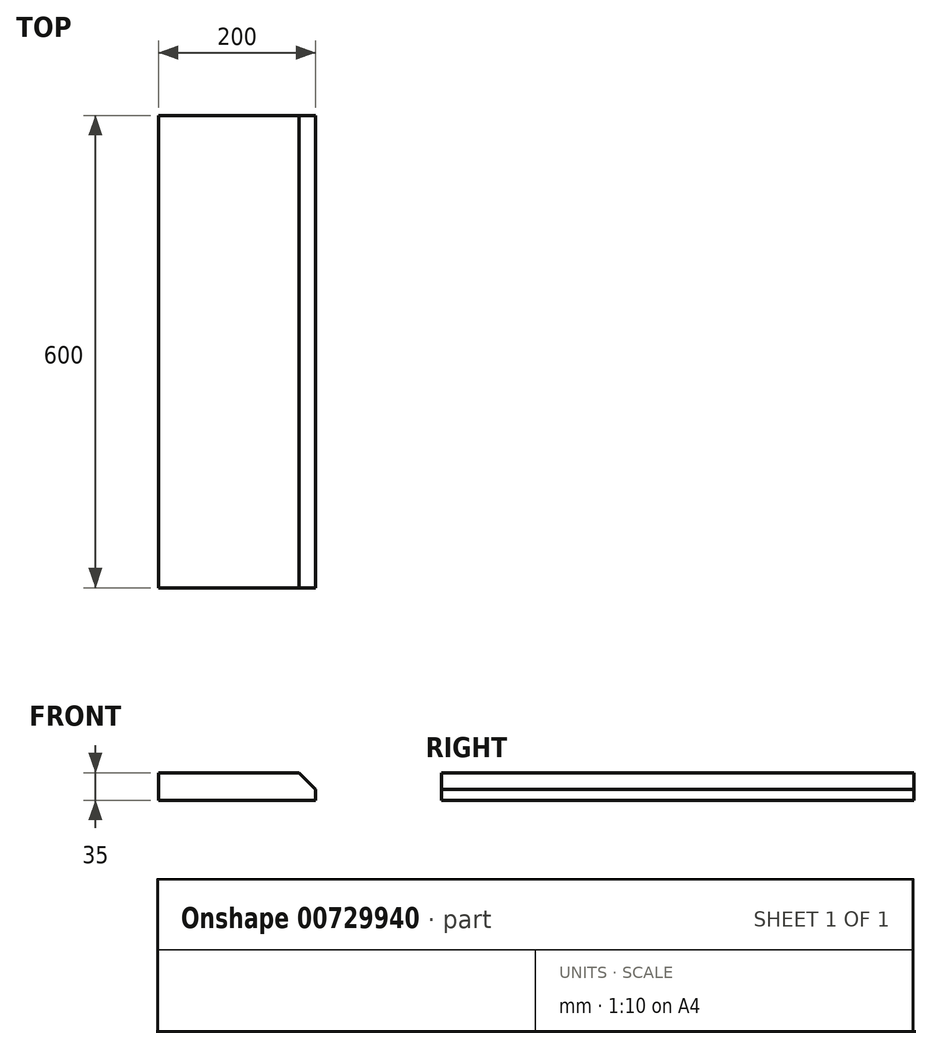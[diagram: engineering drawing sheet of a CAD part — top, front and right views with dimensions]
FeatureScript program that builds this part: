
annotation { "Feature Type Name" : "Feature", "Feature Type Description" : "" }
export const myFeature = defineFeature(function(context is Context, id is Id, definition is map)
    precondition{}
    {
        {
            var Q0;
            Q0=qCreatedBy(makeId("Front.planeOp"),FACE);
            var sketch = newSketch(context, id + "F0", { "sketchPlane" : qUnion([Q0])});
            skLineSegment(sketch, "E0", {"start": v(122, -16) * mm, "end": v(-78, -16) * mm});
            skLineSegment(sketch, "E1", {"start": v(-78, -16) * mm, "end": v(-78, 19) * mm});
            skLineSegment(sketch, "E2", {"start": v(-78, 19) * mm, "end": v(101, 19) * mm});
            skLineSegment(sketch, "E3", {"start": v(101, 19) * mm, "end": v(122, -2) * mm});
            skLineSegment(sketch, "E4", {"start": v(122, -2) * mm, "end": v(122, -16) * mm});
            skSolve(sketch);
        }
        {
            var Q0;
            Q0=makeQuery(id+"F0.imprint","IMPRINT",FACE,{"disambiguationData":[TD([[makeQuery(id+"F0.imprint","IMPRINT",EDGE,{"derivedFrom":sQuery(id+"F0.wireOp",EDGE,"E0")}),-1.0]])]});
            extrude(context, id + "F1", {"entities" : qUnion([Q0]), "depth" : 600 * mm, "offsetDistance" : 25 * mm, "symmetric" : true});
        }
    });
